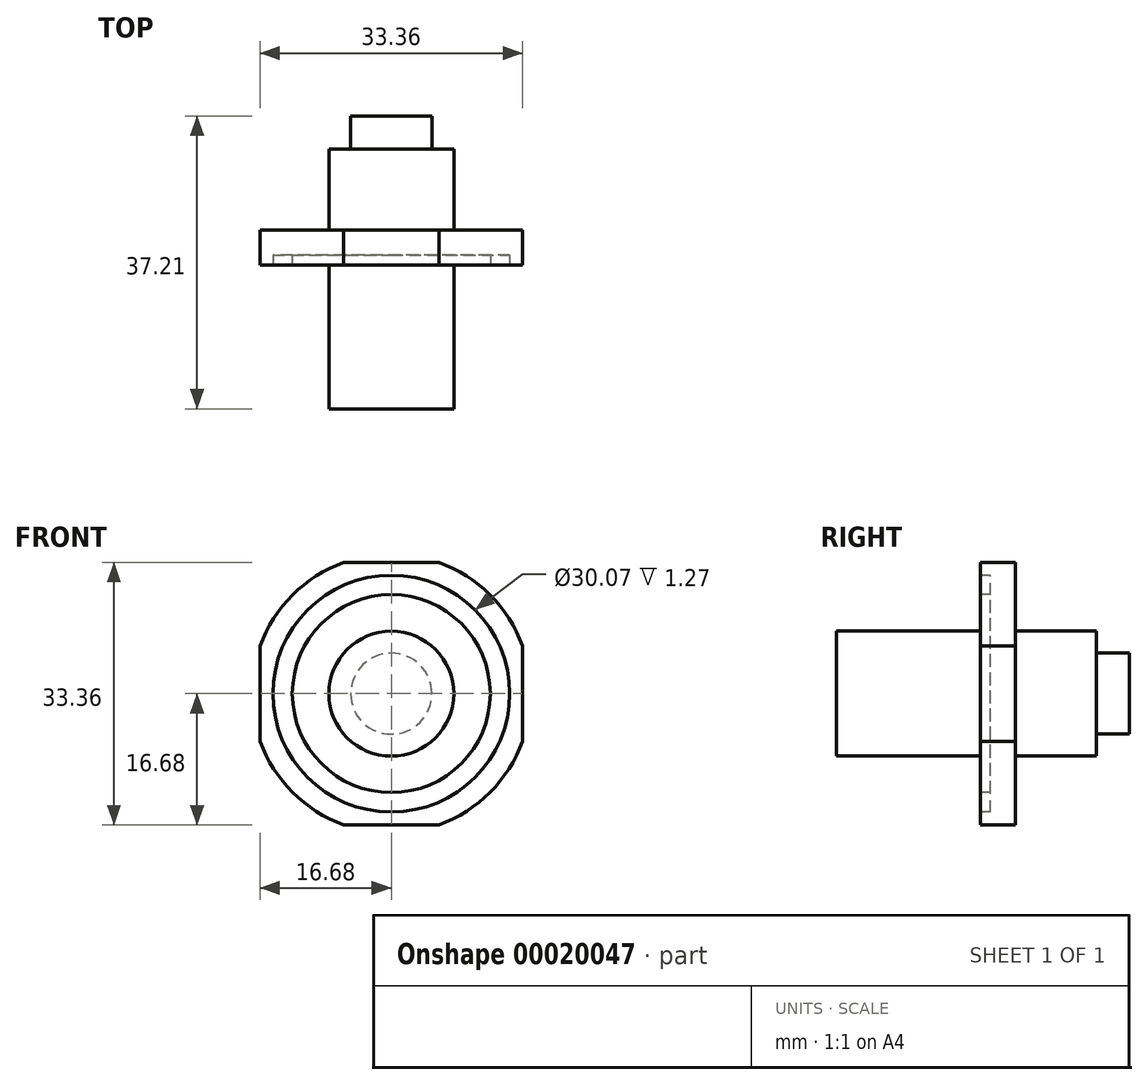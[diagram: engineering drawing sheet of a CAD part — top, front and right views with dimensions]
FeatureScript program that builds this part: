
annotation { "Feature Type Name" : "Feature", "Feature Type Description" : "" }
export const myFeature = defineFeature(function(context is Context, id is Id, definition is map)
    precondition{}
    {
        {
            var Q0;
            Q0=qCreatedBy(makeId("Front.planeOp"),FACE);
            var sketch = newSketch(context, id + "F0", { "sketchPlane" : qUnion([Q0])});
            skCircle(sketch, "E0", {"center": v(0, 0) * mm, "radius": 17.74 * mm});
            skSolve(sketch);
        }
        {
            var Q0;
            Q0 = qSketchRegion(id + "F0", true);
            extrude(context, id + "F1", {"entities" : qUnion([Q0]), "oppositeDirection" : true, "depth" : 4.44 * mm});
        }
        {
            var Q0;
            Q0=makeQuery(id+"F1.opExtrude","CAP_FACE",FACE,{"disambiguationData":[OSD([sQuery(id+"F0.wireOp",EDGE,"E0")])],"isStart":true});
            var sketch = newSketch(context, id + "F2", { "sketchPlane" : qUnion([Q0])});
            skCircle(sketch, "E1", {"center": v(0, 0) * mm, "radius": 7.94 * mm});
            skSolve(sketch);
        }
        {
            var Q0;
            Q0 = qSketchRegion(id + "F2", true);
            extrude(context, id + "F3", {"entities" : qUnion([Q0]), "operationType" : NewBodyOperationType.ADD, "depth" : 18.29 * mm});
        }
        {
            var Q0;
            Q0=makeQuery(id+"F1.opExtrude","CAP_FACE",FACE,{"disambiguationData":[OSD([sQuery(id+"F0.wireOp",EDGE,"E0")])],"isStart":false});
            var sketch = newSketch(context, id + "F4", { "sketchPlane" : qUnion([Q0])});
            skCircle(sketch, "E2", {"center": v(0, 0) * mm, "radius": 7.94 * mm});
            skSolve(sketch);
        }
        {
            var Q0;
            Q0 = qSketchRegion(id + "F4", true);
            extrude(context, id + "F5", {"entities" : qUnion([Q0]), "operationType" : NewBodyOperationType.ADD, "depth" : 10.29 * mm});
        }
        {
            var Q0;
            Q0=makeQuery(id+"F5.opExtrude","CAP_FACE",FACE,{"disambiguationData":[OSD([sQuery(id+"F4.wireOp",EDGE,"E2")])],"isStart":false});
            var sketch = newSketch(context, id + "F6", { "sketchPlane" : qUnion([Q0])});
            skCircle(sketch, "E3", {"center": v(0, 0) * mm, "radius": 5.14 * mm});
            skSolve(sketch);
        }
        {
            var Q0;
            Q0 = qSketchRegion(id + "F6", true);
            extrude(context, id + "F7", {"entities" : qUnion([Q0]), "operationType" : NewBodyOperationType.ADD, "depth" : 4.2 * mm});
        }
        {
            var Q0;
            Q0=makeQuery(id+"F1.opExtrude","CAP_FACE",FACE,{"disambiguationData":[OSD([sQuery(id+"F0.wireOp",EDGE,"E0")])],"isStart":true});
            var sketch = newSketch(context, id + "F8", { "sketchPlane" : qUnion([Q0])});
            skLineSegment(sketch, "E4.rect.bottom", {"start": v(16.68, -16.68) * mm, "end": v(-16.68, -16.68) * mm});
            skLineSegment(sketch, "E4.rect.top", {"start": v(16.68, 16.68) * mm, "end": v(-16.68, 16.68) * mm});
            skLineSegment(sketch, "E4.rect.left", {"start": v(16.68, -16.68) * mm, "end": v(16.68, 16.68) * mm});
            skLineSegment(sketch, "E4.rect.right", {"start": v(-16.68, -16.68) * mm, "end": v(-16.68, 16.68) * mm});
            skPoint(sketch, "E4.rect.middle", {"position": v(0, 0) * mm});
            skCircle(sketch, "E5", {"center": v(0, 0) * mm, "radius": 25.4 * mm});
            skSolve(sketch);
        }
        {
            var Q0;
            Q0 = qSketchRegion(id + "F8", true);
            extrude(context, id + "F9", {"entities" : qUnion([Q0]), "operationType" : NewBodyOperationType.REMOVE, "oppositeDirection" : true, "depth" : 25.4 * mm});
        }
        {
            var Q0;
            Q0=makeQuery(id+"F1.opExtrude","CAP_FACE",FACE,{"disambiguationData":[OSD([sQuery(id+"F0.wireOp",EDGE,"E0")])],"isStart":true});
            var sketch = newSketch(context, id + "F10", { "sketchPlane" : qUnion([Q0])});
            skCircle(sketch, "E6", {"center": v(0, 0) * mm, "radius": 15.04 * mm});
            skCircle(sketch, "E7", {"center": v(0, 0) * mm, "radius": 12.57 * mm});
            skSolve(sketch);
        }
        {
            var Q0;
            Q0 = qSketchRegion(id + "F10", true);
            extrude(context, id + "F11", {"entities" : qUnion([Q0]), "operationType" : NewBodyOperationType.REMOVE, "oppositeDirection" : true, "depth" : 1.27 * mm});
        }
    });
